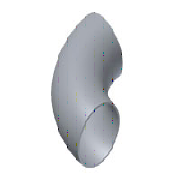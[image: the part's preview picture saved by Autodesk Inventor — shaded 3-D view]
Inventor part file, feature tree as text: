
AUTODESK INVENTOR PART (.ipt)
format: ipt  version: 2023.2 (Build 272271030, 271C)  size: 179,200 bytes
history: native  units: mm
features: other x4, sketch x2, sweep x1
ambient origin geometry x8: Origin, YZ Plane, XZ Plane, XY Plane, X Axis, Y Axis, Z Axis, Center Point
bodies: Solid1 (feature_tree)
feature tree (7):
  sweep  "Sweep1"
  other  "Work Axis1"
  other  "Work Axis2"
  sketch  "Sketch1"  dims[d2=89.0mm d3=3.5mm]
  sketch  "Sketch2"  dims[d4=120.0mm d5=240.0mm d6=0.0mm d7=90.0deg d8=0.0mm]
  other  "Work Point1"
  other  "Work Point2"
